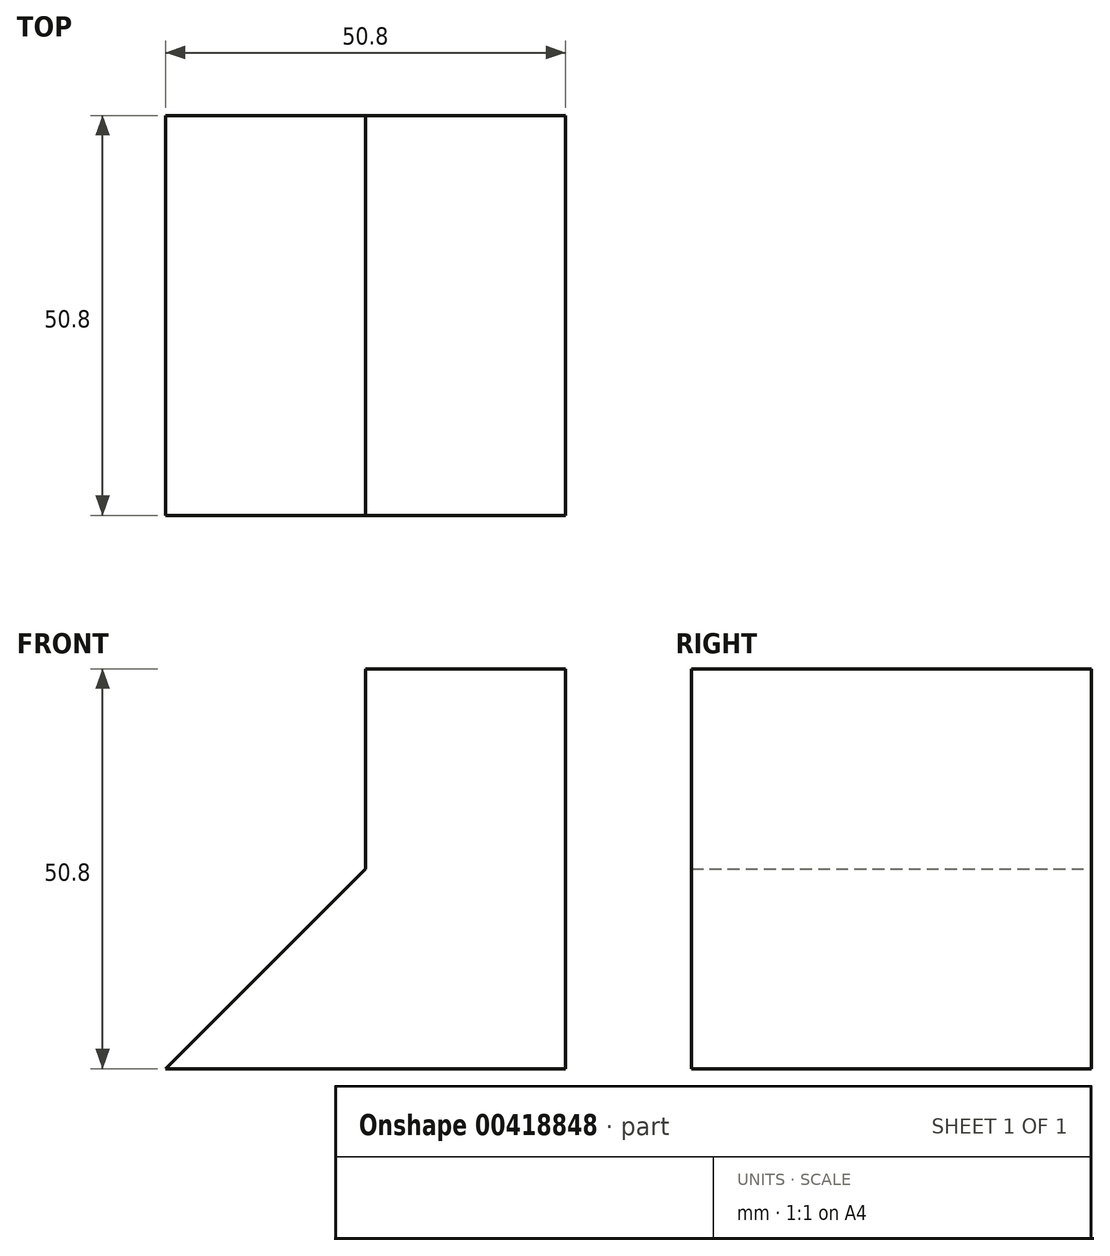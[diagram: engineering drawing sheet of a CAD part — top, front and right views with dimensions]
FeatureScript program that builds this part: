
annotation { "Feature Type Name" : "Feature", "Feature Type Description" : "" }
export const myFeature = defineFeature(function(context is Context, id is Id, definition is map)
    precondition{}
    {
        {
            var Q0;
            Q0=qCreatedBy(makeId("Front.planeOp"),FACE);
            var sketch = newSketch(context, id + "F0", { "sketchPlane" : qUnion([Q0])});
            skLineSegment(sketch, "E0", {"start": v(-50.8, 0) * mm, "end": v(0, 0) * mm});
            skLineSegment(sketch, "E1", {"start": v(0, 0) * mm, "end": v(0, 50.8) * mm});
            skLineSegment(sketch, "E2", {"start": v(0, 50.8) * mm, "end": v(-25.4, 50.8) * mm});
            skLineSegment(sketch, "E3", {"start": v(-25.4, 50.8) * mm, "end": v(-25.4, 25.4) * mm});
            skLineSegment(sketch, "E4", {"start": v(-50.8, 0) * mm, "end": v(-25.4, 25.4) * mm});
            skSolve(sketch);
        }
        {
            var Q0;
            Q0 = qSketchRegion(id + "F0", true);
            extrude(context, id + "F1", {"entities" : qUnion([Q0]), "depth" : 50.8 * mm});
        }
    });
